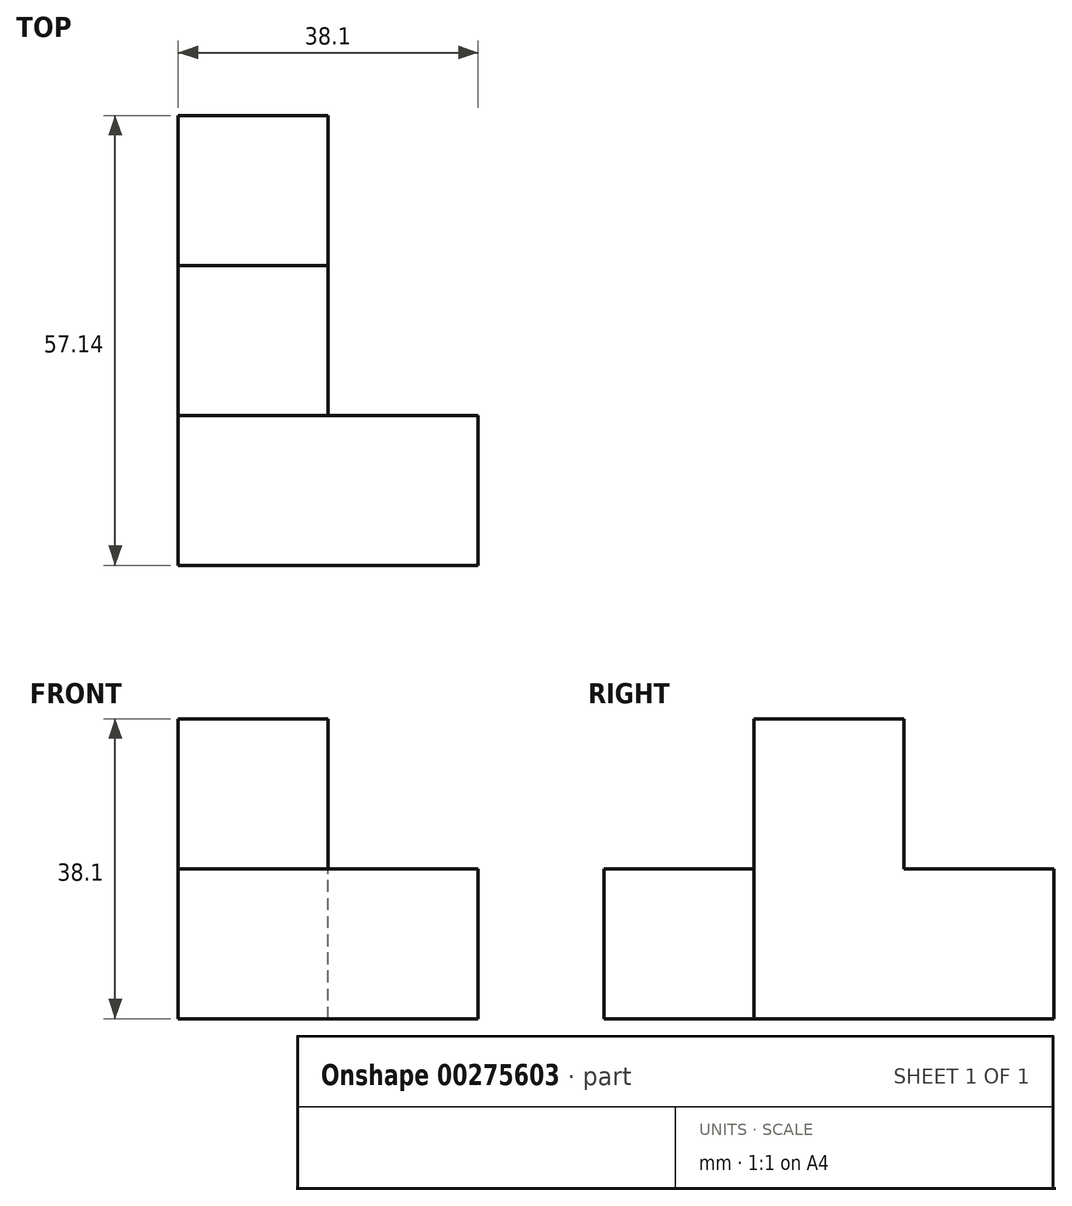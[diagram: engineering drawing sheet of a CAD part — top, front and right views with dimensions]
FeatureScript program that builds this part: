
annotation { "Feature Type Name" : "Feature", "Feature Type Description" : "" }
export const myFeature = defineFeature(function(context is Context, id is Id, definition is map)
    precondition{}
    {
        {
            var Q0;
            Q0=qCreatedBy(makeId("Right.planeOp"),FACE);
            var sketch = newSketch(context, id + "F0", { "sketchPlane" : qUnion([Q0])});
            skLineSegment(sketch, "E0.bottom", {"start": v(-9.52, 9.53) * mm, "end": v(9.53, 9.53) * mm});
            skLineSegment(sketch, "E0.top", {"start": v(-9.52, -9.53) * mm, "end": v(9.52, -9.53) * mm});
            skLineSegment(sketch, "E0.left", {"start": v(-9.53, 9.53) * mm, "end": v(-9.53, -9.52) * mm});
            skLineSegment(sketch, "E0.right", {"start": v(9.53, 9.53) * mm, "end": v(9.53, -9.53) * mm});
            skPoint(sketch, "E0.middle", {"position": v(0, 0) * mm});
            skLineSegment(sketch, "E1", {"start": v(9.53, 9.53) * mm, "end": v(28.58, 9.53) * mm});
            skLineSegment(sketch, "E2", {"start": v(28.58, -9.53) * mm, "end": v(9.53, -9.53) * mm});
            skLineSegment(sketch, "E3", {"start": v(28.58, -9.53) * mm, "end": v(28.58, 9.52) * mm});
            skLineSegment(sketch, "E4", {"start": v(-9.53, 9.53) * mm, "end": v(-28.58, 9.53) * mm});
            skLineSegment(sketch, "E5", {"start": v(-28.58, 9.52) * mm, "end": v(-28.58, -9.52) * mm});
            skLineSegment(sketch, "E6", {"start": v(-28.58, -9.53) * mm, "end": v(-9.53, -9.53) * mm});
            skLineSegment(sketch, "E7", {"start": v(-9.53, 9.53) * mm, "end": v(-9.53, 28.57) * mm});
            skLineSegment(sketch, "E8", {"start": v(9.52, 28.57) * mm, "end": v(-9.53, 28.57) * mm});
            skLineSegment(sketch, "E9", {"start": v(9.53, 28.57) * mm, "end": v(9.53, 9.53) * mm});
            skSolve(sketch);
        }
        {
            var Q0;
            Q0=makeQuery(id+"F0.imprint","IMPRINT",FACE,{"disambiguationData":[TD([[makeQuery(id+"F0.imprint","IMPRINT",EDGE,{"derivedFrom":sQuery(id+"F0.wireOp",EDGE,"E0.bottom")}),-1.0]])]});
            var Q1;
            Q1=makeQuery(id+"F0.imprint","IMPRINT",FACE,{"disambiguationData":[TD([[makeQuery(id+"F0.imprint","IMPRINT",EDGE,{"derivedFrom":sQuery(id+"F0.wireOp",EDGE,"E0.bottom")}),1.0]])]});
            var Q2;
            Q2=makeQuery(id+"F0.imprint","IMPRINT",FACE,{"disambiguationData":[TD([[makeQuery(id+"F0.imprint","IMPRINT",EDGE,{"derivedFrom":sQuery(id+"F0.wireOp",EDGE,"E0.right")}),1.0]])]});
            extrude(context, id + "F1", {"entities" : qUnion([Q0, Q1, Q2]), "depth" : 19.05 * mm});
        }
        {
            var Q0;
            Q0=makeQuery(id+"F0.imprint","IMPRINT",FACE,{"disambiguationData":[TD([[makeQuery(id+"F0.imprint","IMPRINT",EDGE,{"derivedFrom":sQuery(id+"F0.wireOp",EDGE,"E0.left")}),-1.0]])]});
            extrude(context, id + "F2", {"entities" : qUnion([Q0]), "operationType" : NewBodyOperationType.ADD, "depth" : 38.1 * mm});
        }
    });
